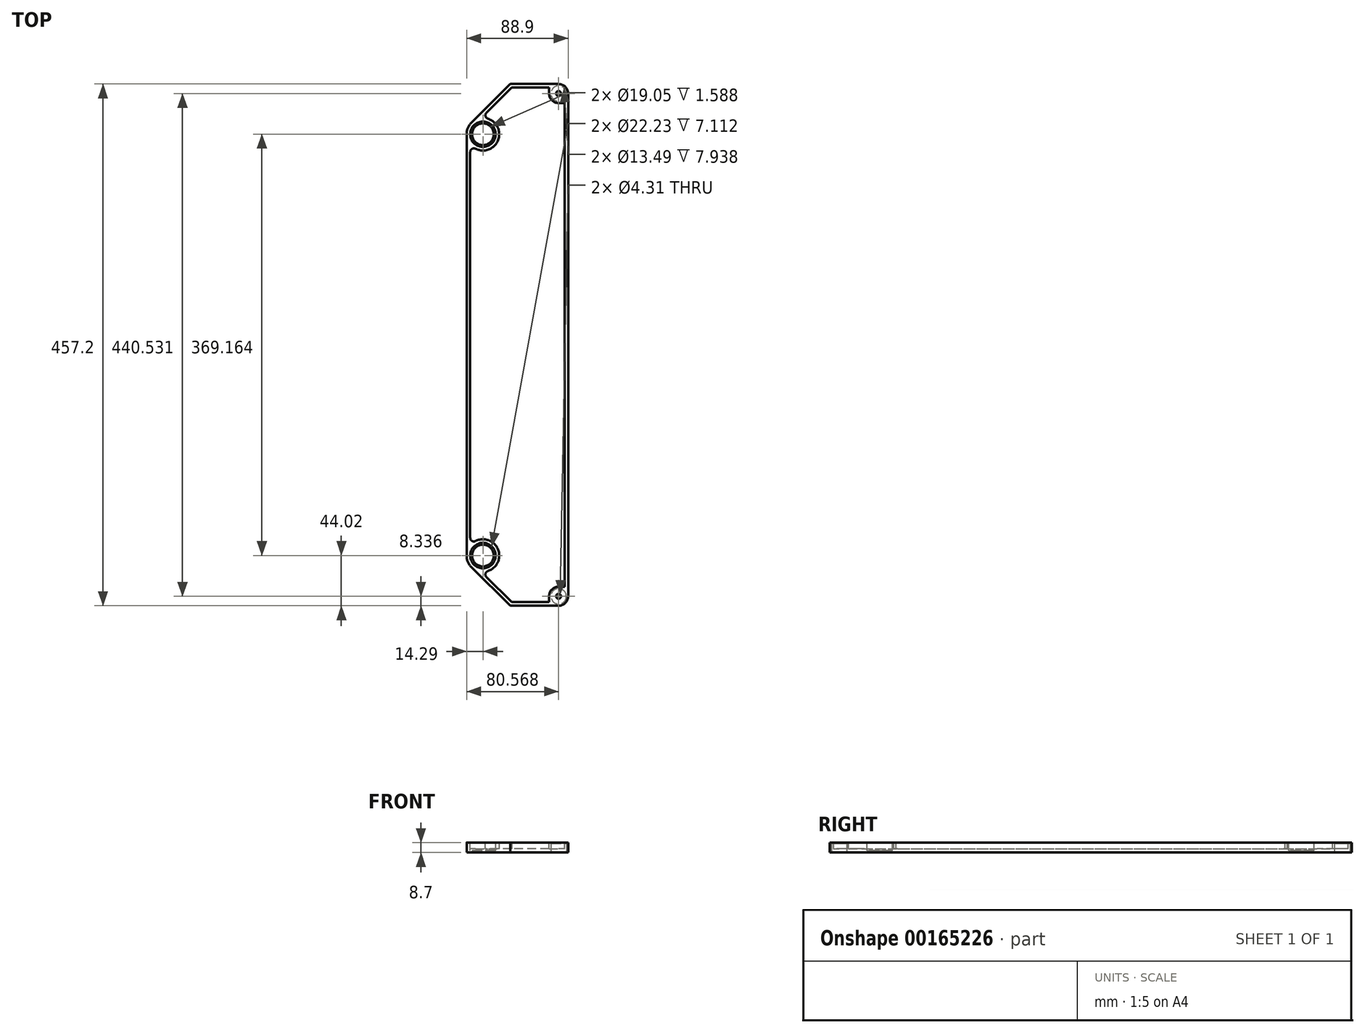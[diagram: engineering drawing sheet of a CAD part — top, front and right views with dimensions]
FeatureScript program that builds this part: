
annotation { "Feature Type Name" : "Feature", "Feature Type Description" : "" }
export const myFeature = defineFeature(function(context is Context, id is Id, definition is map)
    precondition{}
    {
        {
            var Q0;
            Q0=qCreatedBy(makeId("Top.planeOp"),FACE);
            var sketch = newSketch(context, id + "F0", { "sketchPlane" : qUnion([Q0])});
            skCircle(sketch, "E0", {"center": v(0, 0) * mm, "radius": 9.53 * mm});
            skArc(sketch, "E1", {"start": v(-14.29, 0) * mm, "mid": v(-13.2, -5.47) * mm, "end": v(-10.1, -10.1) * mm});
            skLineSegment(sketch, "E2", {"start": v(-14.29, 0) * mm, "end": v(-14.29, 369.16) * mm});
            skArc(sketch, "E3", {"start": v(-10.1, 379.27) * mm, "mid": v(-13.2, 374.63) * mm, "end": v(-14.29, 369.16) * mm});
            skCircle(sketch, "E4", {"center": v(0, 369.16) * mm, "radius": 9.53 * mm});
            skLineSegment(sketch, "E5", {"start": v(-10.1, -10.1) * mm, "end": v(23.81, -44.02) * mm});
            skLineSegment(sketch, "E6", {"start": v(23.81, -44.02) * mm, "end": v(74.61, -44.02) * mm});
            skLineSegment(sketch, "E7", {"start": v(74.61, -44.02) * mm, "end": v(74.61, 413.18) * mm});
            skLineSegment(sketch, "E8", {"start": v(74.61, 413.18) * mm, "end": v(23.81, 413.18) * mm});
            skLineSegment(sketch, "E9", {"start": v(23.81, 413.18) * mm, "end": v(-10.1, 379.27) * mm});
            skLineSegment(sketch, "E10", {"start": v(-14.29, 184.58) * mm, "end": v(23.81, 184.58) * mm, "construction": true});
            skLineSegment(sketch, "E11", {"start": v(23.81, -44.02) * mm, "end": v(23.81, 413.18) * mm, "construction": true});
            skSolve(sketch);
        }
        {
            var Q0;
            Q0 = qSketchRegion(id + "F0", true);
            extrude(context, id + "F1", {"entities" : qUnion([Q0]), "depth" : 8.7 * mm});
        }
        {
            var Q0;
            Q0=makeQuery(id+"F1.opExtrude","CAP_FACE",FACE,{"disambiguationData":[OSD([sQuery(id+"F0.wireOp",EDGE,"E0"),sQuery(id+"F0.wireOp",EDGE,"E1"),sQuery(id+"F0.wireOp",EDGE,"E2"),sQuery(id+"F0.wireOp",EDGE,"E3"),sQuery(id+"F0.wireOp",EDGE,"E4"),sQuery(id+"F0.wireOp",EDGE,"E5"),sQuery(id+"F0.wireOp",EDGE,"E6"),sQuery(id+"F0.wireOp",EDGE,"E7"),sQuery(id+"F0.wireOp",EDGE,"E8"),sQuery(id+"F0.wireOp",EDGE,"E9")])],"isStart":false});
            var sketch = newSketch(context, id + "F2", { "sketchPlane" : qUnion([Q0])});
            skCircle(sketch, "E12", {"center": v(0, 369.16) * mm, "radius": 11.11 * mm});
            skCircle(sketch, "E13", {"center": v(0, 0) * mm, "radius": 11.11 * mm});
            skSolve(sketch);
        }
        {
            var Q0;
            Q0 = qSketchRegion(id + "F2", true);
            extrude(context, id + "F3", {"entities" : qUnion([Q0]), "operationType" : NewBodyOperationType.REMOVE, "oppositeDirection" : true, "depth" : 7.11 * mm});
        }
        {
            var Q0;
            Q0=makeQuery(id+"F1.opExtrude","CAP_FACE",FACE,{"disambiguationData":[OSD([sQuery(id+"F0.wireOp",EDGE,"E0"),sQuery(id+"F0.wireOp",EDGE,"E1"),sQuery(id+"F0.wireOp",EDGE,"E2"),sQuery(id+"F0.wireOp",EDGE,"E3"),sQuery(id+"F0.wireOp",EDGE,"E4"),sQuery(id+"F0.wireOp",EDGE,"E5"),sQuery(id+"F0.wireOp",EDGE,"E6"),sQuery(id+"F0.wireOp",EDGE,"E7"),sQuery(id+"F0.wireOp",EDGE,"E8"),sQuery(id+"F0.wireOp",EDGE,"E9")])],"isStart":false});
            shell(context, id + "F4", {"entities" : qUnion([Q0]), "thickness" : 3.17 * mm});
        }
        {
            var Q0;
            Q0=makeQuery(id+"F4.opShell","TWEAK_EDGE",EDGE,{"derivedFrom":[makeQuery(id+"F1.opExtrude","SWEPT_FACE",FACE,{"disambiguationData":[OSD([sQuery(id+"F0.wireOp",EDGE,"E5")])]}),makeQuery(id+"F3.boolean.opBoolean","COPY",FACE,{"derivedFrom":makeQuery(id+"F3.opExtrude","SWEPT_FACE",FACE,{"disambiguationData":[OSD([sQuery(id+"F2.wireOp",EDGE,"E13")])]})})]});
            var Q1;
            Q1=makeQuery(id+"F4.opShell","TWEAK_EDGE",EDGE,{"derivedFrom":[makeQuery(id+"F1.opExtrude","SWEPT_FACE",FACE,{"disambiguationData":[OSD([sQuery(id+"F0.wireOp",EDGE,"E2")])]}),makeQuery(id+"F3.boolean.opBoolean","COPY",FACE,{"derivedFrom":makeQuery(id+"F3.opExtrude","SWEPT_FACE",FACE,{"disambiguationData":[OSD([sQuery(id+"F2.wireOp",EDGE,"E13")])]})})]});
            var Q2;
            Q2=makeQuery(id+"F4.opShell","TWEAK_EDGE",EDGE,{"derivedFrom":[makeQuery(id+"F1.opExtrude","SWEPT_FACE",FACE,{"disambiguationData":[OSD([sQuery(id+"F0.wireOp",EDGE,"E2")])]}),makeQuery(id+"F3.boolean.opBoolean","COPY",FACE,{"derivedFrom":makeQuery(id+"F3.opExtrude","SWEPT_FACE",FACE,{"disambiguationData":[OSD([sQuery(id+"F2.wireOp",EDGE,"E12")])]})})]});
            var Q3;
            Q3=makeQuery(id+"F4.opShell","TWEAK_EDGE",EDGE,{"derivedFrom":[makeQuery(id+"F1.opExtrude","SWEPT_FACE",FACE,{"disambiguationData":[OSD([sQuery(id+"F0.wireOp",EDGE,"E9")])]}),makeQuery(id+"F3.boolean.opBoolean","COPY",FACE,{"derivedFrom":makeQuery(id+"F3.opExtrude","SWEPT_FACE",FACE,{"disambiguationData":[OSD([sQuery(id+"F2.wireOp",EDGE,"E12")])]})})]});
            fillet(context, id + "F5", {"entities" : qUnion([Q0, Q1, Q2, Q3]), "radius" : 3.17 * mm, "tangentPropagation" : true, "allowEdgeOverflow" : false});
        }
        {
            var Q0;
            Q0=makeQuery(id+"F4.opShell","OFFSET_FACE",FACE,{"disambiguationData":[OSD([sQuery(id+"F0.wireOp",EDGE,"E0"),sQuery(id+"F0.wireOp",EDGE,"E1"),sQuery(id+"F0.wireOp",EDGE,"E2"),sQuery(id+"F0.wireOp",EDGE,"E3"),sQuery(id+"F0.wireOp",EDGE,"E4"),sQuery(id+"F0.wireOp",EDGE,"E5"),sQuery(id+"F0.wireOp",EDGE,"E6"),sQuery(id+"F0.wireOp",EDGE,"E7"),sQuery(id+"F0.wireOp",EDGE,"E8"),sQuery(id+"F0.wireOp",EDGE,"E9")])]});
            var sketch = newSketch(context, id + "F6", { "sketchPlane" : qUnion([Q0])});
            skLineSegment(sketch, "E14.bottom", {"start": v(74.61, 413.18) * mm, "end": v(57.94, 413.18) * mm});
            skLineSegment(sketch, "E14.top", {"start": v(74.61, 396.51) * mm, "end": v(57.94, 396.51) * mm});
            skLineSegment(sketch, "E14.left", {"start": v(74.61, 413.18) * mm, "end": v(74.61, 396.51) * mm});
            skLineSegment(sketch, "E14.right", {"start": v(57.94, 413.18) * mm, "end": v(57.94, 396.51) * mm});
            skLineSegment(sketch, "E15.bottom", {"start": v(74.61, -44.02) * mm, "end": v(57.94, -44.02) * mm});
            skLineSegment(sketch, "E15.top", {"start": v(74.61, -27.35) * mm, "end": v(57.94, -27.35) * mm});
            skLineSegment(sketch, "E15.left", {"start": v(74.61, -44.02) * mm, "end": v(74.61, -27.35) * mm});
            skLineSegment(sketch, "E15.right", {"start": v(57.94, -44.02) * mm, "end": v(57.94, -27.35) * mm});
            skSolve(sketch);
        }
        {
            var Q0;
            Q0 = qSketchRegion(id + "F6", true);
            var Q1;
            Q1=makeQuery(id+"F1.opExtrude","CAP_FACE",FACE,{"disambiguationData":[OSD([sQuery(id+"F0.wireOp",EDGE,"E0"),sQuery(id+"F0.wireOp",EDGE,"E1"),sQuery(id+"F0.wireOp",EDGE,"E2"),sQuery(id+"F0.wireOp",EDGE,"E3"),sQuery(id+"F0.wireOp",EDGE,"E4"),sQuery(id+"F0.wireOp",EDGE,"E5"),sQuery(id+"F0.wireOp",EDGE,"E6"),sQuery(id+"F0.wireOp",EDGE,"E7"),sQuery(id+"F0.wireOp",EDGE,"E8"),sQuery(id+"F0.wireOp",EDGE,"E9")])],"isStart":false});
            extrude(context, id + "F7", {"entities" : qUnion([Q0]), "operationType" : NewBodyOperationType.ADD, "endBound" : BoundingType.UP_TO_SURFACE, "endBoundEntityFace" : qUnion([Q1]), "depth" : 25.4 * mm});
        }
        {
            var Q0;
            Q0=makeQuery(id+"F1.opExtrude","SWEPT_EDGE",EDGE,{"disambiguationData":[OSD([sQuery(id+"F0.wireOp",EDGE,"E7"),sQuery(id+"F0.wireOp",EDGE,"E8")])]});
            var Q1;
            Q1=makeQuery(id+"F1.opExtrude","SWEPT_EDGE",EDGE,{"disambiguationData":[OSD([sQuery(id+"F0.wireOp",EDGE,"E6"),sQuery(id+"F0.wireOp",EDGE,"E7")])]});
            var Q2;
            Q2=makeQuery(id+"F7.opExtrude","SWEPT_EDGE",EDGE,{"disambiguationData":[OSD([sQuery(id+"F6.wireOp",EDGE,"E15.top"),sQuery(id+"F6.wireOp",EDGE,"E15.right")])]});
            var Q3;
            Q3=makeQuery(id+"F7.opExtrude","SWEPT_EDGE",EDGE,{"disambiguationData":[OSD([sQuery(id+"F6.wireOp",EDGE,"E14.top"),sQuery(id+"F6.wireOp",EDGE,"E14.right")])]});
            fillet(context, id + "F8", {"entities" : qUnion([Q0, Q1, Q2, Q3]), "radius" : 8.33 * mm, "tangentPropagation" : true, "allowEdgeOverflow" : false});
        }
        {
            var Q0;
            Q0=makeQuery(id+"F1.opExtrude","CAP_FACE",FACE,{"disambiguationData":[OSD([sQuery(id+"F0.wireOp",EDGE,"E0"),sQuery(id+"F0.wireOp",EDGE,"E1"),sQuery(id+"F0.wireOp",EDGE,"E2"),sQuery(id+"F0.wireOp",EDGE,"E3"),sQuery(id+"F0.wireOp",EDGE,"E4"),sQuery(id+"F0.wireOp",EDGE,"E5"),sQuery(id+"F0.wireOp",EDGE,"E6"),sQuery(id+"F0.wireOp",EDGE,"E7"),sQuery(id+"F0.wireOp",EDGE,"E8"),sQuery(id+"F0.wireOp",EDGE,"E9")])],"isStart":true});
            var sketch = newSketch(context, id + "F9", { "sketchPlane" : qUnion([Q0])});
            skCircle(sketch, "E16", {"center": v(66.28, 35.68) * mm, "radius": 6.75 * mm});
            skCircle(sketch, "E17", {"center": v(66.28, -404.85) * mm, "radius": 6.75 * mm});
            skSolve(sketch);
        }
        {
            var Q0;
            Q0 = qSketchRegion(id + "F9", true);
            extrude(context, id + "F10", {"entities" : qUnion([Q0]), "operationType" : NewBodyOperationType.REMOVE, "oppositeDirection" : true, "depth" : 7.94 * mm});
        }
        {
            var Q0;
            Q0=makeQuery(id+"F1.opExtrude","CAP_FACE",FACE,{"disambiguationData":[OSD([sQuery(id+"F0.wireOp",EDGE,"E0"),sQuery(id+"F0.wireOp",EDGE,"E1"),sQuery(id+"F0.wireOp",EDGE,"E2"),sQuery(id+"F0.wireOp",EDGE,"E3"),sQuery(id+"F0.wireOp",EDGE,"E4"),sQuery(id+"F0.wireOp",EDGE,"E5"),sQuery(id+"F0.wireOp",EDGE,"E6"),sQuery(id+"F0.wireOp",EDGE,"E7"),sQuery(id+"F0.wireOp",EDGE,"E8"),sQuery(id+"F0.wireOp",EDGE,"E9")])],"isStart":true});
            var sketch = newSketch(context, id + "F11", { "sketchPlane" : qUnion([Q0])});
            skCircle(sketch, "E18", {"center": v(66.28, 35.68) * mm, "radius": 2.15 * mm});
            skCircle(sketch, "E19", {"center": v(66.28, -404.85) * mm, "radius": 2.15 * mm});
            skSolve(sketch);
        }
        {
            var Q0;
            Q0 = qSketchRegion(id + "F11", true);
            var Q1;
            Q1=makeQuery(id+"F7.boolean.opBoolean","MERGE",FACE,{"derivedFrom":[makeQuery(id+"F1.opExtrude","CAP_FACE",FACE,{"disambiguationData":[OSD([sQuery(id+"F0.wireOp",EDGE,"E0"),sQuery(id+"F0.wireOp",EDGE,"E1"),sQuery(id+"F0.wireOp",EDGE,"E2"),sQuery(id+"F0.wireOp",EDGE,"E3"),sQuery(id+"F0.wireOp",EDGE,"E4"),sQuery(id+"F0.wireOp",EDGE,"E5"),sQuery(id+"F0.wireOp",EDGE,"E6"),sQuery(id+"F0.wireOp",EDGE,"E7"),sQuery(id+"F0.wireOp",EDGE,"E8"),sQuery(id+"F0.wireOp",EDGE,"E9")])],"isStart":false}),makeQuery(id+"F7.opExtrude","CAP_FACE",FACE,{"disambiguationData":[OSD([sQuery(id+"F6.wireOp",EDGE,"E14.bottom"),sQuery(id+"F6.wireOp",EDGE,"E14.top"),sQuery(id+"F6.wireOp",EDGE,"E14.left"),sQuery(id+"F6.wireOp",EDGE,"E14.right")])],"isStart":false}),makeQuery(id+"F7.opExtrude","CAP_FACE",FACE,{"disambiguationData":[OSD([sQuery(id+"F6.wireOp",EDGE,"E15.bottom"),sQuery(id+"F6.wireOp",EDGE,"E15.top"),sQuery(id+"F6.wireOp",EDGE,"E15.left"),sQuery(id+"F6.wireOp",EDGE,"E15.right")])],"isStart":false})]});
            extrude(context, id + "F12", {"entities" : qUnion([Q0]), "operationType" : NewBodyOperationType.REMOVE, "endBound" : BoundingType.UP_TO_SURFACE, "oppositeDirection" : true, "endBoundEntityFace" : qUnion([Q1]), "depth" : 25.4 * mm});
        }
    });
